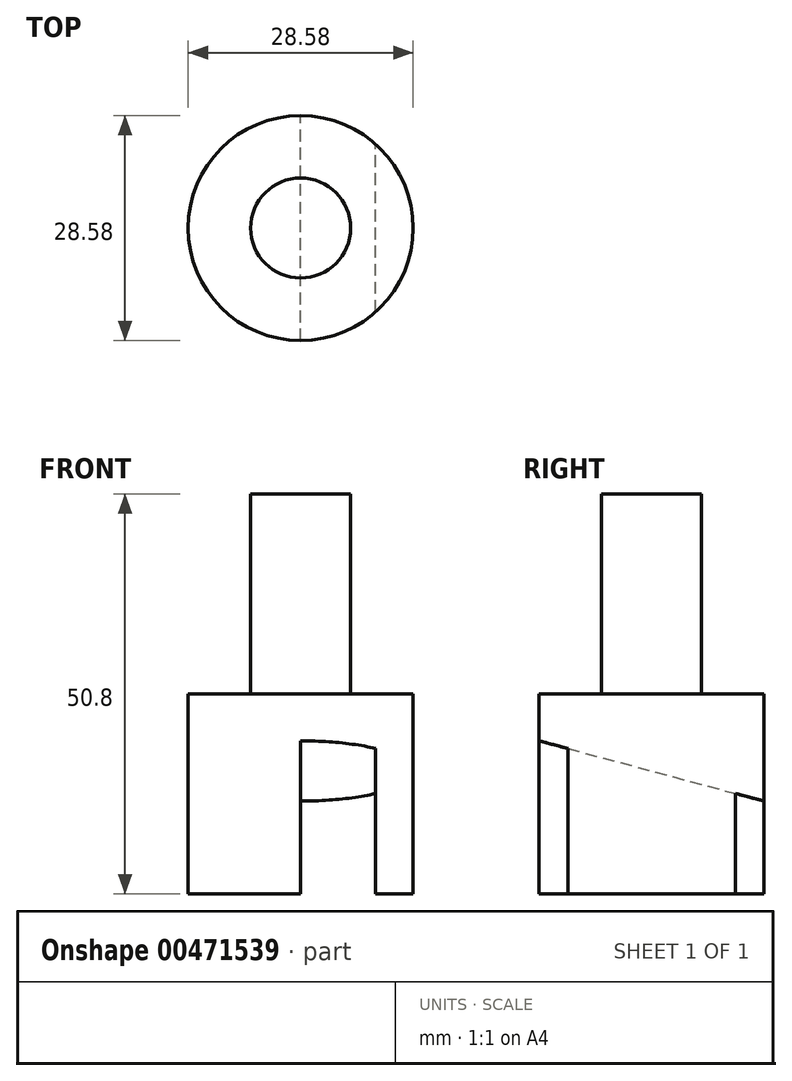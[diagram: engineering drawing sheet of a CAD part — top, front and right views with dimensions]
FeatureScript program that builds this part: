
annotation { "Feature Type Name" : "Feature", "Feature Type Description" : "" }
export const myFeature = defineFeature(function(context is Context, id is Id, definition is map)
    precondition{}
    {
        {
            var Q0;
            Q0=qCreatedBy(makeId("Top.planeOp"),FACE);
            var sketch = newSketch(context, id + "F0", { "sketchPlane" : qUnion([Q0])});
            skCircle(sketch, "E0", {"center": v(0, 0) * mm, "radius": 14.29 * mm});
            skSolve(sketch);
        }
        {
            var Q0;
            Q0=makeQuery(id+"F0.imprint","IMPRINT",FACE,{"disambiguationData":[TD([[makeQuery(id+"F0.imprint","IMPRINT",EDGE,{"derivedFrom":sQuery(id+"F0.wireOp",EDGE,"E0")}),1.0]])]});
            extrude(context, id + "F1", {"entities" : qUnion([Q0]), "depth" : 25.4 * mm});
        }
        {
            var Q0;
            Q0=makeQuery(id+"F1.opExtrude","CAP_FACE",FACE,{"disambiguationData":[OSD([sQuery(id+"F0.wireOp",EDGE,"E0")])],"isStart":false});
            var sketch = newSketch(context, id + "F2", { "sketchPlane" : qUnion([Q0])});
            skCircle(sketch, "E1", {"center": v(0, 0) * mm, "radius": 6.35 * mm});
            skSolve(sketch);
        }
        {
            var Q0;
            Q0=makeQuery(id+"F2.imprint","IMPRINT",FACE,{"disambiguationData":[TD([[makeQuery(id+"F2.imprint","IMPRINT",EDGE,{"derivedFrom":sQuery(id+"F2.wireOp",EDGE,"E1")}),1.0]])]});
            extrude(context, id + "F3", {"entities" : qUnion([Q0]), "operationType" : NewBodyOperationType.ADD, "depth" : 25.4 * mm});
        }
        {
            var Q0;
            Q0=makeQuery(id+"F1.opExtrude","CAP_FACE",FACE,{"disambiguationData":[OSD([sQuery(id+"F0.wireOp",EDGE,"E0")])],"isStart":true});
            var sketch = newSketch(context, id + "F4", { "sketchPlane" : qUnion([Q0])});
            skLineSegment(sketch, "E2", {"start": v(-9.63, 30.12) * mm, "end": v(-9.63, -31.23) * mm});
            skSolve(sketch);
        }
        {
            var Q0;
            Q0=makeQuery(id+"F1.opExtrude","CAP_FACE",FACE,{"disambiguationData":[OSD([sQuery(id+"F0.wireOp",EDGE,"E0")])],"isStart":false});
            var sketch = newSketch(context, id + "F5", { "sketchPlane" : qUnion([Q0])});
            skLineSegment(sketch, "E3", {"start": v(-14.29, -25.1) * mm, "end": v(-14.29, 32.15) * mm});
            skSolve(sketch);
        }
        {
            var Q0;
            Q0=qCreatedBy(makeId("Right.planeOp"),FACE);
            var sketch = newSketch(context, id + "F6", { "sketchPlane" : qUnion([Q0])});
            skLineSegment(sketch, "E4", {"start": v(-11.11, 0) * mm, "end": v(11.1, 0) * mm});
            skLineSegment(sketch, "E5", {"start": v(-14.29, 19.45) * mm, "end": v(14.29, 11.8) * mm});
            skLineSegment(sketch, "E6", {"start": v(-14.29, 0) * mm, "end": v(-14.29, 19.45) * mm});
            skLineSegment(sketch, "E7", {"start": v(14.29, 11.8) * mm, "end": v(14.29, 0) * mm});
            skLineSegment(sketch, "E8.top", {"start": v(-14.29, 0) * mm, "end": v(14.29, 0) * mm});
            skLineSegment(sketch, "E8.left", {"start": v(-14.29, 19.45) * mm, "end": v(-14.29, 0) * mm});
            skLineSegment(sketch, "E9", {"start": v(14.29, 0) * mm, "end": v(14.29, 11.8) * mm});
            skSolve(sketch);
        }
        {
            var Q0;
            Q0 = qSketchRegion(id + "F6", true);
            extrude(context, id + "F7", {"entities" : qUnion([Q0]), "operationType" : NewBodyOperationType.REMOVE, "depth" : 9.52 * mm});
        }
    });
